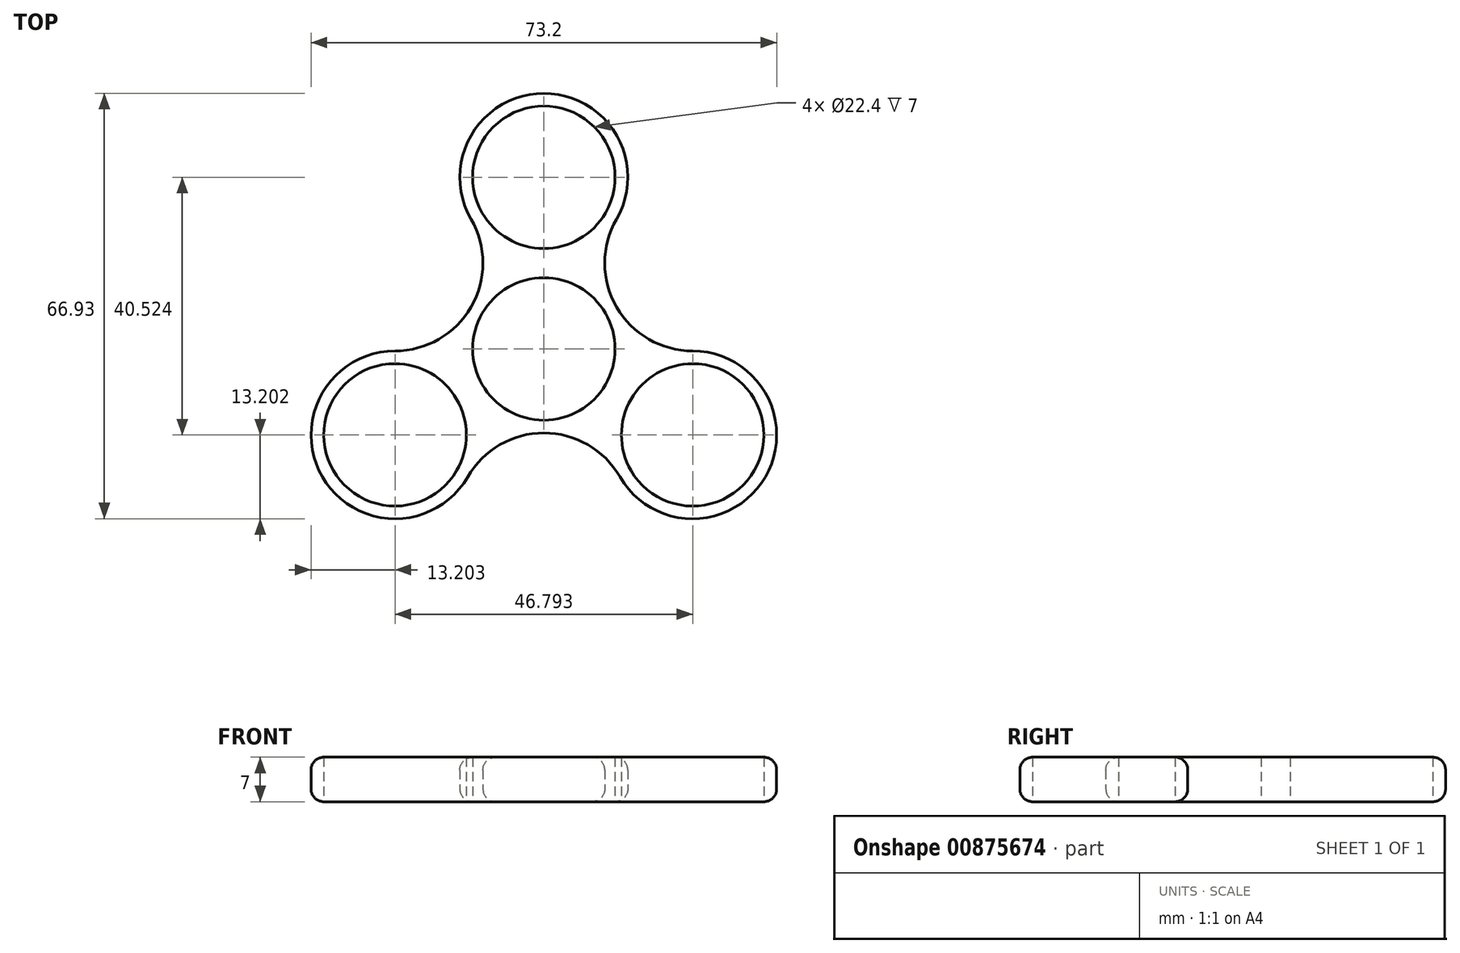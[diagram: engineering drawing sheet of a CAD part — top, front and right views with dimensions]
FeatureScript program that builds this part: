
annotation { "Feature Type Name" : "Feature", "Feature Type Description" : "" }
export const myFeature = defineFeature(function(context is Context, id is Id, definition is map)
    precondition{}
    {
        {
            var Q0;
            Q0=qCreatedBy(makeId("Top.planeOp"),FACE);
            var sketch = newSketch(context, id + "F0", { "sketchPlane" : qUnion([Q0])});
            skCircle(sketch, "E0", {"center": v(0, 0) * mm, "radius": 11.2 * mm});
            skCircle(sketch, "E1", {"center": v(0, 27.02) * mm, "radius": 11.2 * mm});
            skArc(sketch, "E2", {"start": v(11.43, 20.42) * mm, "mid": v(0, 40.22) * mm, "end": v(-11.43, 20.42) * mm});
            skArc(sketch, "E3.1.0", {"start": v(-23.4, -0.3) * mm, "mid": v(-34.83, -20.1) * mm, "end": v(-11.97, -20.1) * mm});
            skCircle(sketch, "E3.1.1", {"center": v(-23.4, -13.5) * mm, "radius": 11.2 * mm});
            skArc(sketch, "E3.2.0", {"start": v(11.97, -20.1) * mm, "mid": v(34.83, -20.1) * mm, "end": v(23.4, -0.3) * mm});
            skCircle(sketch, "E3.2.1", {"center": v(23.4, -13.5) * mm, "radius": 11.2 * mm});
            skLineSegment(sketch, "E4", {"start": v(0, 0) * mm, "end": v(23.4, -13.5) * mm, "construction": true});
            skLineSegment(sketch, "E5", {"start": v(0, 27.02) * mm, "end": v(0, 0) * mm, "construction": true});
            skLineSegment(sketch, "E6", {"start": v(-23.4, -13.5) * mm, "end": v(0, 0) * mm, "construction": true});
            skArc(sketch, "E7", {"start": v(11.43, 20.42) * mm, "mid": v(11.43, 6.6) * mm, "end": v(23.4, -0.3) * mm});
            skArc(sketch, "E8.1.0", {"start": v(-23.4, -0.3) * mm, "mid": v(-11.43, 6.6) * mm, "end": v(-11.43, 20.42) * mm});
            skArc(sketch, "E8.2.0", {"start": v(11.97, -20.1) * mm, "mid": v(0, -13.2) * mm, "end": v(-11.97, -20.1) * mm});
            skSolve(sketch);
        }
        {
            var Q0;
            Q0=qSketchRegion(id+"F0",true);
            extrude(context, id + "F1", {"entities" : qUnion([Q0]), "depth" : 7 * mm, "offsetDistance" : 25 * mm});
        }
        {
            var Q0;
            Q0=makeQuery(id+"F1.opExtrude","CAP_EDGE",EDGE,{"disambiguationData":[OSD([sQuery(id+"F0.wireOp",EDGE,"E3.1.0")])],"isStart":false});
            var Q1;
            Q1=makeQuery(id+"F1.opExtrude","CAP_EDGE",EDGE,{"disambiguationData":[OSD([sQuery(id+"F0.wireOp",EDGE,"E8.2.0")])],"isStart":false});
            var Q2;
            Q2=makeQuery(id+"F1.opExtrude","CAP_EDGE",EDGE,{"disambiguationData":[OSD([sQuery(id+"F0.wireOp",EDGE,"E3.2.0")])],"isStart":false});
            var Q3;
            Q3=makeQuery(id+"F1.opExtrude","CAP_EDGE",EDGE,{"disambiguationData":[OSD([sQuery(id+"F0.wireOp",EDGE,"E7")])],"isStart":false});
            var Q4;
            Q4=makeQuery(id+"F1.opExtrude","CAP_EDGE",EDGE,{"disambiguationData":[OSD([sQuery(id+"F0.wireOp",EDGE,"E2")])],"isStart":false});
            var Q5;
            Q5=makeQuery(id+"F1.opExtrude","CAP_EDGE",EDGE,{"disambiguationData":[OSD([sQuery(id+"F0.wireOp",EDGE,"E8.1.0")])],"isStart":false});
            var Q6;
            Q6=makeQuery(id+"F1.opExtrude","CAP_EDGE",EDGE,{"disambiguationData":[OSD([sQuery(id+"F0.wireOp",EDGE,"E3.2.0")])],"isStart":true});
            var Q7;
            Q7=makeQuery(id+"F1.opExtrude","CAP_EDGE",EDGE,{"disambiguationData":[OSD([sQuery(id+"F0.wireOp",EDGE,"E7")])],"isStart":true});
            var Q8;
            Q8=makeQuery(id+"F1.opExtrude","CAP_EDGE",EDGE,{"disambiguationData":[OSD([sQuery(id+"F0.wireOp",EDGE,"E2")])],"isStart":true});
            var Q9;
            Q9=makeQuery(id+"F1.opExtrude","CAP_EDGE",EDGE,{"disambiguationData":[OSD([sQuery(id+"F0.wireOp",EDGE,"E8.1.0")])],"isStart":true});
            var Q10;
            Q10=makeQuery(id+"F1.opExtrude","CAP_EDGE",EDGE,{"disambiguationData":[OSD([sQuery(id+"F0.wireOp",EDGE,"E3.1.0")])],"isStart":true});
            var Q11;
            Q11=makeQuery(id+"F1.opExtrude","CAP_EDGE",EDGE,{"disambiguationData":[OSD([sQuery(id+"F0.wireOp",EDGE,"E8.2.0")])],"isStart":true});
            fillet(context, id + "F2", {"entities" : qUnion([Q0, Q1, Q2, Q3, Q4, Q5, Q6, Q7, Q8, Q9, Q10, Q11]), "radius" : 2 * mm, "tangentPropagation" : true, "allowEdgeOverflow" : false});
        }
    });
